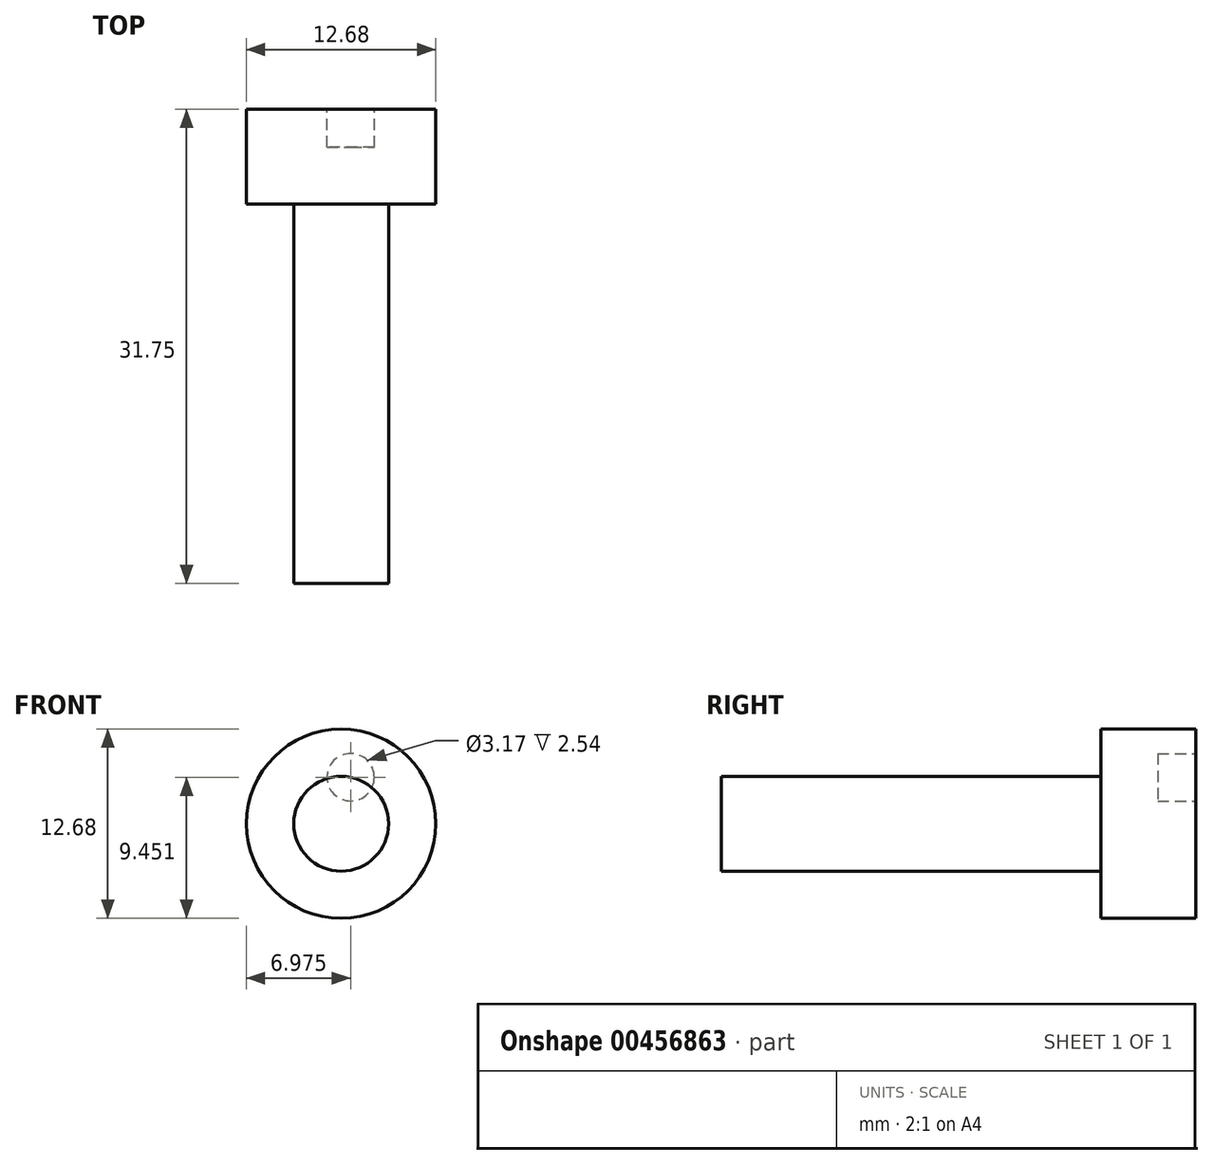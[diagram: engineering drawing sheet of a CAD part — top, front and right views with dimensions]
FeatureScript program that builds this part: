
annotation { "Feature Type Name" : "Feature", "Feature Type Description" : "" }
export const myFeature = defineFeature(function(context is Context, id is Id, definition is map)
    precondition{}
    {
        {
            var Q0;
            Q0=qCreatedBy(makeId("Front.planeOp"),FACE);
            var sketch = newSketch(context, id + "F0", { "sketchPlane" : qUnion([Q0])});
            skCircle(sketch, "E0", {"center": v(0, 0) * mm, "radius": 6.34 * mm});
            skSolve(sketch);
        }
        {
            var Q0;
            Q0=qSketchRegion(id+"F0",true);
            extrude(context, id + "F1", {"entities" : qUnion([Q0]), "depth" : 6.35 * mm});
        }
        {
            var Q0;
            Q0=makeQuery(id+"F1.opExtrude","CAP_FACE",FACE,{"disambiguationData":[OSD([sQuery(id+"F0.wireOp",EDGE,"E0")])],"isStart":false});
            var sketch = newSketch(context, id + "F2", { "sketchPlane" : qUnion([Q0])});
            skCircle(sketch, "E1", {"center": v(0, 0) * mm, "radius": 3.17 * mm});
            skSolve(sketch);
        }
        {
            var Q0;
            Q0=makeQuery(id+"F2.imprint","IMPRINT",FACE,{"disambiguationData":[TD([[makeQuery(id+"F2.imprint","IMPRINT",EDGE,{"derivedFrom":sQuery(id+"F2.wireOp",EDGE,"E1")}),1.0]])]});
            extrude(context, id + "F3", {"entities" : qUnion([Q0]), "operationType" : NewBodyOperationType.ADD, "depth" : 25.4 * mm});
        }
        {
            var Q0;
            Q0=makeQuery(id+"F1.opExtrude","CAP_FACE",FACE,{"disambiguationData":[OSD([sQuery(id+"F0.wireOp",EDGE,"E0")])],"isStart":true});
            var sketch = newSketch(context, id + "F4", { "sketchPlane" : qUnion([Q0])});
            skCircle(sketch, "E2", {"center": v(0, 0) * mm, "radius": 3.18 * mm, "construction": true});
            skCircle(sketch, "E3", {"center": v(-0.64, 3.11) * mm, "radius": 1.59 * mm});
            skSolve(sketch);
        }
        {
            var Q0;
            Q0=makeQuery(id+"F4.imprint","IMPRINT",FACE,{"disambiguationData":[TD([[makeQuery(id+"F4.imprint","IMPRINT",EDGE,{"derivedFrom":sQuery(id+"F4.wireOp",EDGE,"E3")}),1.0]])]});
            extrude(context, id + "F5", {"entities" : qUnion([Q0]), "operationType" : NewBodyOperationType.REMOVE, "oppositeDirection" : true, "depth" : 2.54 * mm});
        }
    });
